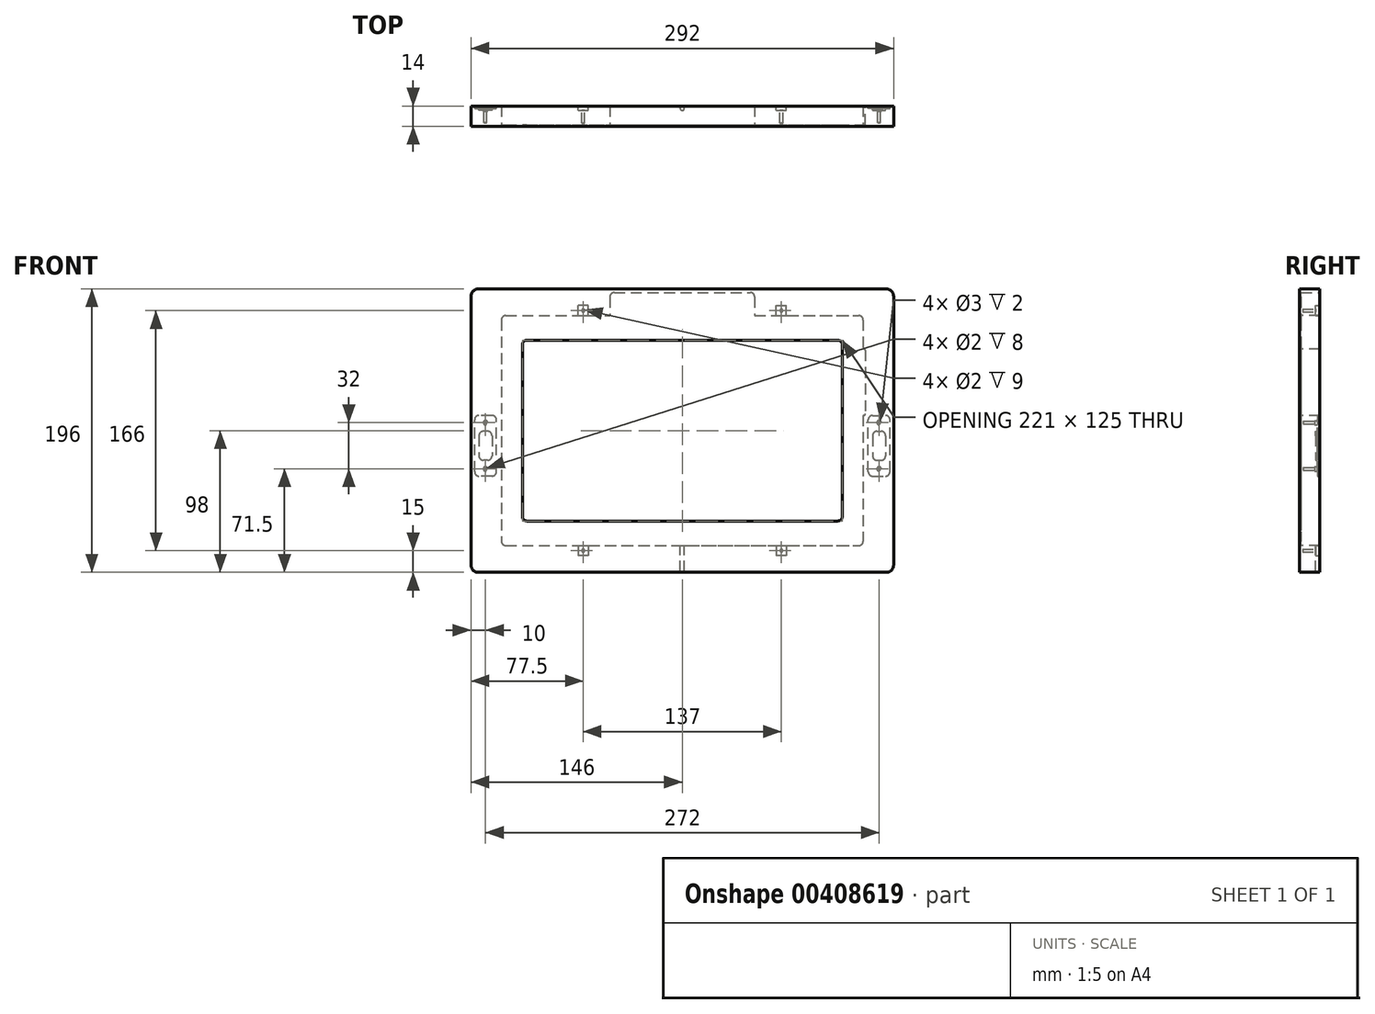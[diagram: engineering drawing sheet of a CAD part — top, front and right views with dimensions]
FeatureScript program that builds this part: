
annotation { "Feature Type Name" : "Feature", "Feature Type Description" : "" }
export const myFeature = defineFeature(function(context is Context, id is Id, definition is map)
    precondition{}
    {
        {
            var Q0;
            Q0=qCreatedBy(makeId("Front.planeOp"),FACE);
            var sketch = newSketch(context, id + "F0", { "sketchPlane" : qUnion([Q0])});
            skLineSegment(sketch, "E0.bottom", {"start": v(-122, 79.5) * mm, "end": v(122, 79.5) * mm});
            skLineSegment(sketch, "E0.top", {"start": v(-122, -79.5) * mm, "end": v(122, -79.5) * mm});
            skLineSegment(sketch, "E0.left", {"start": v(-125, 76.5) * mm, "end": v(-125, -76.5) * mm});
            skLineSegment(sketch, "E0.right", {"start": v(125, 76.5) * mm, "end": v(125, -76.5) * mm});
            skPoint(sketch, "E0.middle", {"position": v(0, 0) * mm});
            skLineSegment(sketch, "E1.bottom", {"start": v(-107.5, 62.5) * mm, "end": v(107.5, 62.5) * mm});
            skLineSegment(sketch, "E1.top", {"start": v(-107.5, -62.5) * mm, "end": v(107.5, -62.5) * mm});
            skLineSegment(sketch, "E1.left", {"start": v(-110.5, 59.5) * mm, "end": v(-110.5, -59.5) * mm});
            skLineSegment(sketch, "E1.right", {"start": v(110.5, 59.5) * mm, "end": v(110.5, -59.5) * mm});
            skLineSegment(sketch, "E2.bottom", {"start": v(-141, 98) * mm, "end": v(141, 98) * mm});
            skLineSegment(sketch, "E2.top", {"start": v(-141, -98) * mm, "end": v(141, -98) * mm});
            skLineSegment(sketch, "E2.left", {"start": v(-146, 93) * mm, "end": v(-146, -93) * mm});
            skLineSegment(sketch, "E2.right", {"start": v(146, 93) * mm, "end": v(146, -93) * mm});
            skPoint(sketch, "E3.visualSharp", {"position": v(146, 98) * mm});
            skArc(sketch, "E3.filletArc", {"start": v(146, 93) * mm, "mid": v(144.54, 96.54) * mm, "end": v(141, 98) * mm});
            skPoint(sketch, "E4.visualSharp", {"position": v(-146, 98) * mm});
            skArc(sketch, "E4.filletArc", {"start": v(-141, 98) * mm, "mid": v(-144.54, 96.54) * mm, "end": v(-146, 93) * mm});
            skPoint(sketch, "E5.visualSharp", {"position": v(-146, -98) * mm});
            skArc(sketch, "E5.filletArc", {"start": v(-146, -93) * mm, "mid": v(-144.54, -96.54) * mm, "end": v(-141, -98) * mm});
            skPoint(sketch, "E6.visualSharp", {"position": v(146, -98) * mm});
            skArc(sketch, "E6.filletArc", {"start": v(141, -98) * mm, "mid": v(144.54, -96.54) * mm, "end": v(146, -93) * mm});
            skPoint(sketch, "E7.visualSharp", {"position": v(125, 79.5) * mm});
            skArc(sketch, "E7.filletArc", {"start": v(125, 76.5) * mm, "mid": v(124.12, 78.62) * mm, "end": v(122, 79.5) * mm});
            skPoint(sketch, "E8.visualSharp", {"position": v(-125, 79.5) * mm});
            skArc(sketch, "E8.filletArc", {"start": v(-122, 79.5) * mm, "mid": v(-124.12, 78.62) * mm, "end": v(-125, 76.5) * mm});
            skPoint(sketch, "E9.visualSharp", {"position": v(-125, -79.5) * mm});
            skArc(sketch, "E9.filletArc", {"start": v(-125, -76.5) * mm, "mid": v(-124.12, -78.62) * mm, "end": v(-122, -79.5) * mm});
            skPoint(sketch, "E10.visualSharp", {"position": v(125, -79.5) * mm});
            skArc(sketch, "E10.filletArc", {"start": v(122, -79.5) * mm, "mid": v(124.12, -78.62) * mm, "end": v(125, -76.5) * mm});
            skPoint(sketch, "E11.visualSharp", {"position": v(110.5, 62.5) * mm});
            skArc(sketch, "E11.filletArc", {"start": v(110.5, 59.5) * mm, "mid": v(109.62, 61.62) * mm, "end": v(107.5, 62.5) * mm});
            skPoint(sketch, "E12.visualSharp", {"position": v(-110.5, 62.5) * mm});
            skArc(sketch, "E12.filletArc", {"start": v(-107.5, 62.5) * mm, "mid": v(-109.62, 61.62) * mm, "end": v(-110.5, 59.5) * mm});
            skPoint(sketch, "E13.visualSharp", {"position": v(-110.5, -62.5) * mm});
            skArc(sketch, "E13.filletArc", {"start": v(-110.5, -59.5) * mm, "mid": v(-109.62, -61.62) * mm, "end": v(-107.5, -62.5) * mm});
            skPoint(sketch, "E14.visualSharp", {"position": v(110.5, -62.5) * mm});
            skArc(sketch, "E14.filletArc", {"start": v(107.5, -62.5) * mm, "mid": v(109.62, -61.62) * mm, "end": v(110.5, -59.5) * mm});
            skSolve(sketch);
        }
        {
            var Q0;
            Q0=makeQuery(id+"F0.imprint","IMPRINT",FACE,{"disambiguationData":[TD([[makeQuery(id+"F0.imprint","IMPRINT",EDGE,{"derivedFrom":sQuery(id+"F0.wireOp",EDGE,"E0.bottom")}),1.0]])]});
            var Q1;
            Q1=makeQuery(id+"F0.imprint","IMPRINT",FACE,{"disambiguationData":[TD([[makeQuery(id+"F0.imprint","IMPRINT",EDGE,{"derivedFrom":sQuery(id+"F0.wireOp",EDGE,"E0.bottom")}),-1.0]])]});
            extrude(context, id + "F1", {"entities" : qUnion([Q0, Q1]), "oppositeDirection" : true, "depth" : 1 * mm});
        }
        {
            var Q0;
            Q0=makeQuery(id+"F0.imprint","IMPRINT",FACE,{"disambiguationData":[TD([[makeQuery(id+"F0.imprint","IMPRINT",EDGE,{"derivedFrom":sQuery(id+"F0.wireOp",EDGE,"E0.bottom")}),1.0]])]});
            extrude(context, id + "F2", {"entities" : qUnion([Q0]), "operationType" : NewBodyOperationType.ADD, "oppositeDirection" : true, "depth" : 14 * mm});
        }
        {
            var Q0;
            Q0=makeQuery(id+"F2.opExtrude","CAP_FACE",FACE,{"disambiguationData":[OSD([sQuery(id+"F0.wireOp",EDGE,"E0.bottom"),sQuery(id+"F0.wireOp",EDGE,"E0.top"),sQuery(id+"F0.wireOp",EDGE,"E0.left"),sQuery(id+"F0.wireOp",EDGE,"E0.right"),sQuery(id+"F0.wireOp",EDGE,"E2.bottom"),sQuery(id+"F0.wireOp",EDGE,"E2.top"),sQuery(id+"F0.wireOp",EDGE,"E2.left"),sQuery(id+"F0.wireOp",EDGE,"E2.right"),sQuery(id+"F0.wireOp",EDGE,"E3.filletArc"),sQuery(id+"F0.wireOp",EDGE,"E4.filletArc"),sQuery(id+"F0.wireOp",EDGE,"E5.filletArc"),sQuery(id+"F0.wireOp",EDGE,"E6.filletArc"),sQuery(id+"F0.wireOp",EDGE,"E7.filletArc"),sQuery(id+"F0.wireOp",EDGE,"E8.filletArc"),sQuery(id+"F0.wireOp",EDGE,"E9.filletArc"),sQuery(id+"F0.wireOp",EDGE,"E10.filletArc")])],"isStart":false});
            var sketch = newSketch(context, id + "F3", { "sketchPlane" : qUnion([Q0])});
            skLineSegment(sketch, "E15.bottom", {"start": v(47, 95.5) * mm, "end": v(-47, 95.5) * mm});
            skLineSegment(sketch, "E15.top", {"start": v(47, 63.5) * mm, "end": v(-47, 63.5) * mm});
            skLineSegment(sketch, "E15.left", {"start": v(50, 92.5) * mm, "end": v(50, 66.5) * mm});
            skLineSegment(sketch, "E15.right", {"start": v(-50, 92.5) * mm, "end": v(-50, 66.5) * mm});
            skPoint(sketch, "E15.middle", {"position": v(0, 79.5) * mm});
            skPoint(sketch, "E16.visualSharp", {"position": v(-50, 95.5) * mm});
            skArc(sketch, "E16.filletArc", {"start": v(-47, 95.5) * mm, "mid": v(-49.12, 94.62) * mm, "end": v(-50, 92.5) * mm});
            skPoint(sketch, "E17.visualSharp", {"position": v(50, 95.5) * mm});
            skArc(sketch, "E17.filletArc", {"start": v(50, 92.5) * mm, "mid": v(49.12, 94.62) * mm, "end": v(47, 95.5) * mm});
            skPoint(sketch, "E18.visualSharp", {"position": v(50, 63.5) * mm});
            skArc(sketch, "E18.filletArc", {"start": v(47, 63.5) * mm, "mid": v(49.12, 64.38) * mm, "end": v(50, 66.5) * mm});
            skPoint(sketch, "E19.visualSharp", {"position": v(-50, 63.5) * mm});
            skArc(sketch, "E19.filletArc", {"start": v(-50, 66.5) * mm, "mid": v(-49.12, 64.38) * mm, "end": v(-47, 63.5) * mm});
            skSolve(sketch);
        }
        {
            var Q0;
            Q0 = qSketchRegion(id + "F3", true);
            extrude(context, id + "F4", {"entities" : qUnion([Q0]), "oppositeDirection" : true, "depth" : 13 * mm});
        }
        {
            var Q0;
            Q0=makeQuery(id+"F4.opExtrude","SWEPT_BODY",BODY,{"disambiguationData":[OSD([sQuery(id+"F3.wireOp",EDGE,"E15.bottom"),sQuery(id+"F3.wireOp",EDGE,"E15.top"),sQuery(id+"F3.wireOp",EDGE,"E15.left"),sQuery(id+"F3.wireOp",EDGE,"E15.right"),sQuery(id+"F3.wireOp",EDGE,"E16.filletArc"),sQuery(id+"F3.wireOp",EDGE,"E17.filletArc"),sQuery(id+"F3.wireOp",EDGE,"E18.filletArc"),sQuery(id+"F3.wireOp",EDGE,"E19.filletArc")])]});
            var Q1;
            Q1=makeQuery(id+"F1.opExtrude","SWEPT_BODY",BODY,{"disambiguationData":[OSD([sQuery(id+"F0.wireOp",EDGE,"E1.bottom"),sQuery(id+"F0.wireOp",EDGE,"E1.top"),sQuery(id+"F0.wireOp",EDGE,"E1.left"),sQuery(id+"F0.wireOp",EDGE,"E1.right"),sQuery(id+"F0.wireOp",EDGE,"E2.bottom"),sQuery(id+"F0.wireOp",EDGE,"E2.top"),sQuery(id+"F0.wireOp",EDGE,"E2.left"),sQuery(id+"F0.wireOp",EDGE,"E2.right"),sQuery(id+"F0.wireOp",EDGE,"E3.filletArc"),sQuery(id+"F0.wireOp",EDGE,"E4.filletArc"),sQuery(id+"F0.wireOp",EDGE,"E5.filletArc"),sQuery(id+"F0.wireOp",EDGE,"E6.filletArc"),sQuery(id+"F0.wireOp",EDGE,"E11.filletArc"),sQuery(id+"F0.wireOp",EDGE,"E12.filletArc"),sQuery(id+"F0.wireOp",EDGE,"E13.filletArc"),sQuery(id+"F0.wireOp",EDGE,"E14.filletArc")])]});
            booleanBodies(context, id + "F5", {"operationType" : BooleanOperationType.SUBTRACTION, "tools" : qUnion([Q0]), "targets" : qUnion([Q1])});
        }
        {
            var Q0;
            Q0=makeQuery(id+"F2.opExtrude","SWEPT_FACE",FACE,{"disambiguationData":[OSD([sQuery(id+"F0.wireOp",EDGE,"E0.top")])]});
            var sketch = newSketch(context, id + "F6", { "sketchPlane" : qUnion([Q0])});
            skLineSegment(sketch, "E20.bottom", {"start": v(0, 11) * mm, "end": v(0, 11) * mm});
            skLineSegment(sketch, "E20.top", {"start": v(-1.5, 17) * mm, "end": v(1.5, 17) * mm});
            skLineSegment(sketch, "E20.left", {"start": v(-1.5, 12.5) * mm, "end": v(-1.5, 17) * mm});
            skLineSegment(sketch, "E20.right", {"start": v(1.5, 12.5) * mm, "end": v(1.5, 17) * mm});
            skPoint(sketch, "E20.middle", {"position": v(0, 14) * mm});
            skPoint(sketch, "E21.visualSharp", {"position": v(1.5, 11) * mm});
            skArc(sketch, "E21.filletArc", {"start": v(0, 11) * mm, "mid": v(1.06, 11.44) * mm, "end": v(1.5, 12.5) * mm});
            skPoint(sketch, "E22.visualSharp", {"position": v(-1.5, 11) * mm});
            skArc(sketch, "E22.filletArc", {"start": v(-1.5, 12.5) * mm, "mid": v(-1.06, 11.44) * mm, "end": v(0, 11) * mm});
            skSolve(sketch);
        }
        {
            var Q0;
            Q0 = qSketchRegion(id + "F6", true);
            extrude(context, id + "F7", {"entities" : qUnion([Q0]), "oppositeDirection" : true, "depth" : 18 * mm});
        }
        {
            var Q0;
            Q0=makeQuery(id+"F7.opExtrude","SWEPT_BODY",BODY,{"disambiguationData":[OSD([sQuery(id+"F6.wireOp",EDGE,"E20.top"),sQuery(id+"F6.wireOp",EDGE,"E20.left"),sQuery(id+"F6.wireOp",EDGE,"E20.right"),sQuery(id+"F6.wireOp",EDGE,"E21.filletArc"),sQuery(id+"F6.wireOp",EDGE,"E22.filletArc")])]});
            var Q1;
            Q1=makeQuery(id+"F1.opExtrude","SWEPT_BODY",BODY,{"disambiguationData":[OSD([sQuery(id+"F0.wireOp",EDGE,"E1.bottom"),sQuery(id+"F0.wireOp",EDGE,"E1.top"),sQuery(id+"F0.wireOp",EDGE,"E1.left"),sQuery(id+"F0.wireOp",EDGE,"E1.right"),sQuery(id+"F0.wireOp",EDGE,"E2.bottom"),sQuery(id+"F0.wireOp",EDGE,"E2.top"),sQuery(id+"F0.wireOp",EDGE,"E2.left"),sQuery(id+"F0.wireOp",EDGE,"E2.right"),sQuery(id+"F0.wireOp",EDGE,"E3.filletArc"),sQuery(id+"F0.wireOp",EDGE,"E4.filletArc"),sQuery(id+"F0.wireOp",EDGE,"E5.filletArc"),sQuery(id+"F0.wireOp",EDGE,"E6.filletArc"),sQuery(id+"F0.wireOp",EDGE,"E11.filletArc"),sQuery(id+"F0.wireOp",EDGE,"E12.filletArc"),sQuery(id+"F0.wireOp",EDGE,"E13.filletArc"),sQuery(id+"F0.wireOp",EDGE,"E14.filletArc")])]});
            booleanBodies(context, id + "F8", {"operationType" : BooleanOperationType.SUBTRACTION, "tools" : qUnion([Q0]), "targets" : qUnion([Q1])});
        }
        {
            var Q0;
            Q0=makeQuery(id+"F2.opExtrude","CAP_FACE",FACE,{"disambiguationData":[OSD([sQuery(id+"F0.wireOp",EDGE,"E0.bottom"),sQuery(id+"F0.wireOp",EDGE,"E0.top"),sQuery(id+"F0.wireOp",EDGE,"E0.left"),sQuery(id+"F0.wireOp",EDGE,"E0.right"),sQuery(id+"F0.wireOp",EDGE,"E2.bottom"),sQuery(id+"F0.wireOp",EDGE,"E2.top"),sQuery(id+"F0.wireOp",EDGE,"E2.left"),sQuery(id+"F0.wireOp",EDGE,"E2.right"),sQuery(id+"F0.wireOp",EDGE,"E3.filletArc"),sQuery(id+"F0.wireOp",EDGE,"E4.filletArc"),sQuery(id+"F0.wireOp",EDGE,"E5.filletArc"),sQuery(id+"F0.wireOp",EDGE,"E6.filletArc"),sQuery(id+"F0.wireOp",EDGE,"E7.filletArc"),sQuery(id+"F0.wireOp",EDGE,"E8.filletArc"),sQuery(id+"F0.wireOp",EDGE,"E9.filletArc"),sQuery(id+"F0.wireOp",EDGE,"E10.filletArc")])],"isStart":false});
            var sketch = newSketch(context, id + "F9", { "sketchPlane" : qUnion([Q0])});
            skLineSegment(sketch, "E23.bottom", {"start": v(-125.5, 56.5) * mm, "end": v(-123.5, 56.5) * mm});
            skLineSegment(sketch, "E23.top", {"start": v(-125.5, 10.5) * mm, "end": v(-123.5, 10.5) * mm});
            skLineSegment(sketch, "E23.left", {"start": v(-126.5, 55.5) * mm, "end": v(-126.5, 11.5) * mm});
            skLineSegment(sketch, "E23.right", {"start": v(-123.5, 56.5) * mm, "end": v(-123.5, 10.5) * mm});
            skPoint(sketch, "E23.middle", {"position": v(-125, 33.5) * mm});
            skPoint(sketch, "E24.visualSharp", {"position": v(-126.5, 56.5) * mm});
            skArc(sketch, "E24.filletArc", {"start": v(-125.5, 56.5) * mm, "mid": v(-126.2, 56.2) * mm, "end": v(-126.5, 55.5) * mm});
            skPoint(sketch, "E25.visualSharp", {"position": v(-126.5, 10.5) * mm});
            skArc(sketch, "E25.filletArc", {"start": v(-126.5, 11.5) * mm, "mid": v(-126.2, 10.8) * mm, "end": v(-125.5, 10.5) * mm});
            skSolve(sketch);
        }
        {
            var Q0;
            Q0 = qSketchRegion(id + "F9", true);
            extrude(context, id + "F10", {"entities" : qUnion([Q0]), "oppositeDirection" : true, "depth" : 13 * mm});
        }
        {
            var Q0;
            Q0=makeQuery(id+"F10.opExtrude","SWEPT_BODY",BODY,{"disambiguationData":[OSD([sQuery(id+"F9.wireOp",EDGE,"E23.bottom"),sQuery(id+"F9.wireOp",EDGE,"E23.top"),sQuery(id+"F9.wireOp",EDGE,"E23.left"),sQuery(id+"F9.wireOp",EDGE,"E23.right"),sQuery(id+"F9.wireOp",EDGE,"E24.filletArc"),sQuery(id+"F9.wireOp",EDGE,"E25.filletArc")])]});
            var Q1;
            Q1=makeQuery(id+"F1.opExtrude","SWEPT_BODY",BODY,{"disambiguationData":[OSD([sQuery(id+"F0.wireOp",EDGE,"E1.bottom"),sQuery(id+"F0.wireOp",EDGE,"E1.top"),sQuery(id+"F0.wireOp",EDGE,"E1.left"),sQuery(id+"F0.wireOp",EDGE,"E1.right"),sQuery(id+"F0.wireOp",EDGE,"E2.bottom"),sQuery(id+"F0.wireOp",EDGE,"E2.top"),sQuery(id+"F0.wireOp",EDGE,"E2.left"),sQuery(id+"F0.wireOp",EDGE,"E2.right"),sQuery(id+"F0.wireOp",EDGE,"E3.filletArc"),sQuery(id+"F0.wireOp",EDGE,"E4.filletArc"),sQuery(id+"F0.wireOp",EDGE,"E5.filletArc"),sQuery(id+"F0.wireOp",EDGE,"E6.filletArc"),sQuery(id+"F0.wireOp",EDGE,"E11.filletArc"),sQuery(id+"F0.wireOp",EDGE,"E12.filletArc"),sQuery(id+"F0.wireOp",EDGE,"E13.filletArc"),sQuery(id+"F0.wireOp",EDGE,"E14.filletArc")])]});
            booleanBodies(context, id + "F11", {"operationType" : BooleanOperationType.SUBTRACTION, "tools" : qUnion([Q0]), "targets" : qUnion([Q1])});
        }
        {
            var Q0;
            Q0=makeQuery(id+"F2.opExtrude","CAP_FACE",FACE,{"disambiguationData":[OSD([sQuery(id+"F0.wireOp",EDGE,"E0.bottom"),sQuery(id+"F0.wireOp",EDGE,"E0.top"),sQuery(id+"F0.wireOp",EDGE,"E0.left"),sQuery(id+"F0.wireOp",EDGE,"E0.right"),sQuery(id+"F0.wireOp",EDGE,"E2.bottom"),sQuery(id+"F0.wireOp",EDGE,"E2.top"),sQuery(id+"F0.wireOp",EDGE,"E2.left"),sQuery(id+"F0.wireOp",EDGE,"E2.right"),sQuery(id+"F0.wireOp",EDGE,"E3.filletArc"),sQuery(id+"F0.wireOp",EDGE,"E4.filletArc"),sQuery(id+"F0.wireOp",EDGE,"E5.filletArc"),sQuery(id+"F0.wireOp",EDGE,"E6.filletArc"),sQuery(id+"F0.wireOp",EDGE,"E7.filletArc"),sQuery(id+"F0.wireOp",EDGE,"E8.filletArc"),sQuery(id+"F0.wireOp",EDGE,"E9.filletArc"),sQuery(id+"F0.wireOp",EDGE,"E10.filletArc")])],"isStart":false});
            var sketch = newSketch(context, id + "F12", { "sketchPlane" : qUnion([Q0])});
            skLineSegment(sketch, "E26.bottom", {"start": v(-131.5, -31.5) * mm, "end": v(-140.5, -31.5) * mm});
            skLineSegment(sketch, "E26.top", {"start": v(-131.5, 10.5) * mm, "end": v(-140.5, 10.5) * mm});
            skLineSegment(sketch, "E26.left", {"start": v(-128.5, -28.5) * mm, "end": v(-128.5, 7.5) * mm});
            skLineSegment(sketch, "E26.right", {"start": v(-143.5, -28.5) * mm, "end": v(-143.5, 7.5) * mm});
            skPoint(sketch, "E26.middle", {"position": v(-136, -10.5) * mm});
            skPoint(sketch, "E27.visualSharp", {"position": v(-143.5, 10.5) * mm});
            skArc(sketch, "E27.filletArc", {"start": v(-140.5, 10.5) * mm, "mid": v(-142.62, 9.62) * mm, "end": v(-143.5, 7.5) * mm});
            skPoint(sketch, "E28.visualSharp", {"position": v(-128.5, 10.5) * mm});
            skArc(sketch, "E28.filletArc", {"start": v(-128.5, 7.5) * mm, "mid": v(-129.38, 9.62) * mm, "end": v(-131.5, 10.5) * mm});
            skPoint(sketch, "E29.visualSharp", {"position": v(-143.5, -31.5) * mm});
            skArc(sketch, "E29.filletArc", {"start": v(-143.5, -28.5) * mm, "mid": v(-142.62, -30.62) * mm, "end": v(-140.5, -31.5) * mm});
            skPoint(sketch, "E30.visualSharp", {"position": v(-128.5, -31.5) * mm});
            skArc(sketch, "E30.filletArc", {"start": v(-131.5, -31.5) * mm, "mid": v(-129.38, -30.62) * mm, "end": v(-128.5, -28.5) * mm});
            skLineSegment(sketch, "E31.bottom", {"start": v(131.5, -31.5) * mm, "end": v(140.5, -31.5) * mm});
            skLineSegment(sketch, "E31.top", {"start": v(131.5, 10.5) * mm, "end": v(140.5, 10.5) * mm});
            skLineSegment(sketch, "E31.left", {"start": v(128.5, -28.5) * mm, "end": v(128.5, 7.5) * mm});
            skLineSegment(sketch, "E31.right", {"start": v(143.5, -28.5) * mm, "end": v(143.5, 7.5) * mm});
            skPoint(sketch, "E31.middle", {"position": v(136, -10.5) * mm});
            skPoint(sketch, "E32.visualSharp", {"position": v(128.5, 10.5) * mm});
            skArc(sketch, "E32.filletArc", {"start": v(131.5, 10.5) * mm, "mid": v(129.38, 9.62) * mm, "end": v(128.5, 7.5) * mm});
            skPoint(sketch, "E33.visualSharp", {"position": v(143.5, 10.5) * mm});
            skArc(sketch, "E33.filletArc", {"start": v(143.5, 7.5) * mm, "mid": v(142.62, 9.62) * mm, "end": v(140.5, 10.5) * mm});
            skPoint(sketch, "E34.visualSharp", {"position": v(143.5, -31.5) * mm});
            skArc(sketch, "E34.filletArc", {"start": v(140.5, -31.5) * mm, "mid": v(142.62, -30.62) * mm, "end": v(143.5, -28.5) * mm});
            skPoint(sketch, "E35.visualSharp", {"position": v(128.5, -31.5) * mm});
            skArc(sketch, "E35.filletArc", {"start": v(128.5, -28.5) * mm, "mid": v(129.38, -30.62) * mm, "end": v(131.5, -31.5) * mm});
            skSolve(sketch);
        }
        {
            var Q0;
            Q0 = qSketchRegion(id + "F12", true);
            extrude(context, id + "F13", {"entities" : qUnion([Q0]), "oppositeDirection" : true, "depth" : 1.59 * mm});
        }
        {
            var Q0;
            Q0=makeQuery(id+"F13.opExtrude","SWEPT_BODY",BODY,{"disambiguationData":[OSD([sQuery(id+"F12.wireOp",EDGE,"E26.bottom"),sQuery(id+"F12.wireOp",EDGE,"E26.top"),sQuery(id+"F12.wireOp",EDGE,"E26.left"),sQuery(id+"F12.wireOp",EDGE,"E26.right"),sQuery(id+"F12.wireOp",EDGE,"E27.filletArc"),sQuery(id+"F12.wireOp",EDGE,"E28.filletArc"),sQuery(id+"F12.wireOp",EDGE,"E29.filletArc"),sQuery(id+"F12.wireOp",EDGE,"E30.filletArc")])]});
            var Q1;
            Q1=makeQuery(id+"F13.opExtrude","SWEPT_BODY",BODY,{"disambiguationData":[OSD([sQuery(id+"F12.wireOp",EDGE,"E31.bottom"),sQuery(id+"F12.wireOp",EDGE,"E31.top"),sQuery(id+"F12.wireOp",EDGE,"E31.left"),sQuery(id+"F12.wireOp",EDGE,"E31.right"),sQuery(id+"F12.wireOp",EDGE,"E32.filletArc"),sQuery(id+"F12.wireOp",EDGE,"E33.filletArc"),sQuery(id+"F12.wireOp",EDGE,"E34.filletArc"),sQuery(id+"F12.wireOp",EDGE,"E35.filletArc")])]});
            var Q2;
            Q2=makeQuery(id+"F1.opExtrude","SWEPT_BODY",BODY,{"disambiguationData":[OSD([sQuery(id+"F0.wireOp",EDGE,"E1.bottom"),sQuery(id+"F0.wireOp",EDGE,"E1.top"),sQuery(id+"F0.wireOp",EDGE,"E1.left"),sQuery(id+"F0.wireOp",EDGE,"E1.right"),sQuery(id+"F0.wireOp",EDGE,"E2.bottom"),sQuery(id+"F0.wireOp",EDGE,"E2.top"),sQuery(id+"F0.wireOp",EDGE,"E2.left"),sQuery(id+"F0.wireOp",EDGE,"E2.right"),sQuery(id+"F0.wireOp",EDGE,"E3.filletArc"),sQuery(id+"F0.wireOp",EDGE,"E4.filletArc"),sQuery(id+"F0.wireOp",EDGE,"E5.filletArc"),sQuery(id+"F0.wireOp",EDGE,"E6.filletArc"),sQuery(id+"F0.wireOp",EDGE,"E11.filletArc"),sQuery(id+"F0.wireOp",EDGE,"E12.filletArc"),sQuery(id+"F0.wireOp",EDGE,"E13.filletArc"),sQuery(id+"F0.wireOp",EDGE,"E14.filletArc")])]});
            booleanBodies(context, id + "F14", {"operationType" : BooleanOperationType.SUBTRACTION, "tools" : qUnion([Q0, Q1]), "targets" : qUnion([Q2])});
        }
        {
            var Q0;
            Q0=makeQuery(id+"F14.opBoolean","COPY",FACE,{"derivedFrom":makeQuery(id+"F13.opExtrude","CAP_FACE",FACE,{"disambiguationData":[OSD([sQuery(id+"F12.wireOp",EDGE,"E26.bottom"),sQuery(id+"F12.wireOp",EDGE,"E26.top"),sQuery(id+"F12.wireOp",EDGE,"E26.left"),sQuery(id+"F12.wireOp",EDGE,"E26.right"),sQuery(id+"F12.wireOp",EDGE,"E27.filletArc"),sQuery(id+"F12.wireOp",EDGE,"E28.filletArc"),sQuery(id+"F12.wireOp",EDGE,"E29.filletArc"),sQuery(id+"F12.wireOp",EDGE,"E30.filletArc")])],"isStart":false})});
            var sketch = newSketch(context, id + "F15", { "sketchPlane" : qUnion([Q0])});
            skLineSegment(sketch, "E36.bottom", {"start": v(-134.5, -0.5) * mm, "end": v(-137.5, -0.5) * mm});
            skLineSegment(sketch, "E36.top", {"start": v(-134.5, -20.5) * mm, "end": v(-137.5, -20.5) * mm});
            skLineSegment(sketch, "E36.left", {"start": v(-131.5, -3.5) * mm, "end": v(-131.5, -17.5) * mm});
            skLineSegment(sketch, "E36.right", {"start": v(-140.5, -3.5) * mm, "end": v(-140.5, -17.5) * mm});
            skPoint(sketch, "E36.middle", {"position": v(-136, -10.5) * mm});
            skPoint(sketch, "E37.visualSharp", {"position": v(-140.5, -0.5) * mm});
            skArc(sketch, "E37.filletArc", {"start": v(-137.5, -0.5) * mm, "mid": v(-139.62, -1.38) * mm, "end": v(-140.5, -3.5) * mm});
            skPoint(sketch, "E38.visualSharp", {"position": v(-131.5, -0.5) * mm});
            skArc(sketch, "E38.filletArc", {"start": v(-131.5, -3.5) * mm, "mid": v(-132.38, -1.38) * mm, "end": v(-134.5, -0.5) * mm});
            skPoint(sketch, "E39.visualSharp", {"position": v(-131.5, -20.5) * mm});
            skArc(sketch, "E39.filletArc", {"start": v(-134.5, -20.5) * mm, "mid": v(-132.38, -19.62) * mm, "end": v(-131.5, -17.5) * mm});
            skPoint(sketch, "E40.visualSharp", {"position": v(-140.5, -20.5) * mm});
            skArc(sketch, "E40.filletArc", {"start": v(-140.5, -17.5) * mm, "mid": v(-139.62, -19.62) * mm, "end": v(-137.5, -20.5) * mm});
            skLineSegment(sketch, "E41.bottom", {"start": v(134.5, -0.5) * mm, "end": v(137.5, -0.5) * mm});
            skLineSegment(sketch, "E41.top", {"start": v(134.5, -20.5) * mm, "end": v(137.5, -20.5) * mm});
            skLineSegment(sketch, "E41.left", {"start": v(131.5, -3.5) * mm, "end": v(131.5, -17.5) * mm});
            skLineSegment(sketch, "E41.right", {"start": v(140.5, -3.5) * mm, "end": v(140.5, -17.5) * mm});
            skPoint(sketch, "E41.middle", {"position": v(136, -10.5) * mm});
            skPoint(sketch, "E42.visualSharp", {"position": v(131.5, -0.5) * mm});
            skArc(sketch, "E42.filletArc", {"start": v(134.5, -0.5) * mm, "mid": v(132.38, -1.38) * mm, "end": v(131.5, -3.5) * mm});
            skPoint(sketch, "E43.visualSharp", {"position": v(131.5, -20.5) * mm});
            skArc(sketch, "E43.filletArc", {"start": v(131.5, -17.5) * mm, "mid": v(132.38, -19.62) * mm, "end": v(134.5, -20.5) * mm});
            skPoint(sketch, "E44.visualSharp", {"position": v(140.5, -20.5) * mm});
            skArc(sketch, "E44.filletArc", {"start": v(137.5, -20.5) * mm, "mid": v(139.62, -19.62) * mm, "end": v(140.5, -17.5) * mm});
            skPoint(sketch, "E45.visualSharp", {"position": v(140.5, -0.5) * mm});
            skArc(sketch, "E45.filletArc", {"start": v(140.5, -3.5) * mm, "mid": v(139.62, -1.38) * mm, "end": v(137.5, -0.5) * mm});
            skSolve(sketch);
        }
        {
            var Q0;
            Q0 = qSketchRegion(id + "F15", true);
            extrude(context, id + "F16", {"entities" : qUnion([Q0]), "oppositeDirection" : true, "depth" : 1.5 * mm});
        }
        {
            var Q0;
            Q0=makeQuery(id+"F16.opExtrude","SWEPT_BODY",BODY,{"disambiguationData":[OSD([sQuery(id+"F15.wireOp",EDGE,"E36.bottom"),sQuery(id+"F15.wireOp",EDGE,"E36.top"),sQuery(id+"F15.wireOp",EDGE,"E36.left"),sQuery(id+"F15.wireOp",EDGE,"E36.right"),sQuery(id+"F15.wireOp",EDGE,"E37.filletArc"),sQuery(id+"F15.wireOp",EDGE,"E38.filletArc"),sQuery(id+"F15.wireOp",EDGE,"E39.filletArc"),sQuery(id+"F15.wireOp",EDGE,"E40.filletArc")])]});
            var Q1;
            Q1=makeQuery(id+"F16.opExtrude","SWEPT_BODY",BODY,{"disambiguationData":[OSD([sQuery(id+"F15.wireOp",EDGE,"E41.bottom"),sQuery(id+"F15.wireOp",EDGE,"E41.top"),sQuery(id+"F15.wireOp",EDGE,"E41.left"),sQuery(id+"F15.wireOp",EDGE,"E41.right"),sQuery(id+"F15.wireOp",EDGE,"E42.filletArc"),sQuery(id+"F15.wireOp",EDGE,"E43.filletArc"),sQuery(id+"F15.wireOp",EDGE,"E44.filletArc"),sQuery(id+"F15.wireOp",EDGE,"E45.filletArc")])]});
            var Q2;
            Q2=makeQuery(id+"F1.opExtrude","SWEPT_BODY",BODY,{"disambiguationData":[OSD([sQuery(id+"F0.wireOp",EDGE,"E1.bottom"),sQuery(id+"F0.wireOp",EDGE,"E1.top"),sQuery(id+"F0.wireOp",EDGE,"E1.left"),sQuery(id+"F0.wireOp",EDGE,"E1.right"),sQuery(id+"F0.wireOp",EDGE,"E2.bottom"),sQuery(id+"F0.wireOp",EDGE,"E2.top"),sQuery(id+"F0.wireOp",EDGE,"E2.left"),sQuery(id+"F0.wireOp",EDGE,"E2.right"),sQuery(id+"F0.wireOp",EDGE,"E3.filletArc"),sQuery(id+"F0.wireOp",EDGE,"E4.filletArc"),sQuery(id+"F0.wireOp",EDGE,"E5.filletArc"),sQuery(id+"F0.wireOp",EDGE,"E6.filletArc"),sQuery(id+"F0.wireOp",EDGE,"E11.filletArc"),sQuery(id+"F0.wireOp",EDGE,"E12.filletArc"),sQuery(id+"F0.wireOp",EDGE,"E13.filletArc"),sQuery(id+"F0.wireOp",EDGE,"E14.filletArc")])]});
            booleanBodies(context, id + "F17", {"operationType" : BooleanOperationType.SUBTRACTION, "tools" : qUnion([Q0, Q1]), "targets" : qUnion([Q2])});
        }
        {
            var Q0;
            Q0=makeQuery(id+"F14.opBoolean","COPY",FACE,{"derivedFrom":makeQuery(id+"F13.opExtrude","CAP_FACE",FACE,{"disambiguationData":[OSD([sQuery(id+"F12.wireOp",EDGE,"E26.bottom"),sQuery(id+"F12.wireOp",EDGE,"E26.top"),sQuery(id+"F12.wireOp",EDGE,"E26.left"),sQuery(id+"F12.wireOp",EDGE,"E26.right"),sQuery(id+"F12.wireOp",EDGE,"E27.filletArc"),sQuery(id+"F12.wireOp",EDGE,"E28.filletArc"),sQuery(id+"F12.wireOp",EDGE,"E29.filletArc"),sQuery(id+"F12.wireOp",EDGE,"E30.filletArc")])],"isStart":false})});
            var sketch = newSketch(context, id + "F18", { "sketchPlane" : qUnion([Q0])});
            skCircle(sketch, "E46", {"center": v(-136, 5.5) * mm, "radius": 1 * mm});
            skCircle(sketch, "E47", {"center": v(-136, -26.5) * mm, "radius": 1 * mm});
            skCircle(sketch, "E48", {"center": v(136, 5.5) * mm, "radius": 1 * mm});
            skCircle(sketch, "E49", {"center": v(136, -26.5) * mm, "radius": 1 * mm});
            skSolve(sketch);
        }
        {
            var Q0;
            Q0 = qSketchRegion(id + "F18", true);
            extrude(context, id + "F19", {"entities" : qUnion([Q0]), "oppositeDirection" : true, "depth" : 10 * mm});
        }
        {
            var Q0;
            Q0=makeQuery(id+"F19.opExtrude","SWEPT_BODY",BODY,{"disambiguationData":[OSD([sQuery(id+"F18.wireOp",EDGE,"E46")])]});
            var Q1;
            Q1=makeQuery(id+"F19.opExtrude","SWEPT_BODY",BODY,{"disambiguationData":[OSD([sQuery(id+"F18.wireOp",EDGE,"E47")])]});
            var Q2;
            Q2=makeQuery(id+"F19.opExtrude","SWEPT_BODY",BODY,{"disambiguationData":[OSD([sQuery(id+"F18.wireOp",EDGE,"E48")])]});
            var Q3;
            Q3=makeQuery(id+"F19.opExtrude","SWEPT_BODY",BODY,{"disambiguationData":[OSD([sQuery(id+"F18.wireOp",EDGE,"E49")])]});
            var Q4;
            Q4=makeQuery(id+"F1.opExtrude","SWEPT_BODY",BODY,{"disambiguationData":[OSD([sQuery(id+"F0.wireOp",EDGE,"E1.bottom"),sQuery(id+"F0.wireOp",EDGE,"E1.top"),sQuery(id+"F0.wireOp",EDGE,"E1.left"),sQuery(id+"F0.wireOp",EDGE,"E1.right"),sQuery(id+"F0.wireOp",EDGE,"E2.bottom"),sQuery(id+"F0.wireOp",EDGE,"E2.top"),sQuery(id+"F0.wireOp",EDGE,"E2.left"),sQuery(id+"F0.wireOp",EDGE,"E2.right"),sQuery(id+"F0.wireOp",EDGE,"E3.filletArc"),sQuery(id+"F0.wireOp",EDGE,"E4.filletArc"),sQuery(id+"F0.wireOp",EDGE,"E5.filletArc"),sQuery(id+"F0.wireOp",EDGE,"E6.filletArc"),sQuery(id+"F0.wireOp",EDGE,"E11.filletArc"),sQuery(id+"F0.wireOp",EDGE,"E12.filletArc"),sQuery(id+"F0.wireOp",EDGE,"E13.filletArc"),sQuery(id+"F0.wireOp",EDGE,"E14.filletArc")])]});
            booleanBodies(context, id + "F20", {"operationType" : BooleanOperationType.SUBTRACTION, "tools" : qUnion([Q0, Q1, Q2, Q3]), "targets" : qUnion([Q4])});
        }
        {
            var Q0;
            Q0=makeQuery(id+"F14.opBoolean","COPY",FACE,{"derivedFrom":makeQuery(id+"F13.opExtrude","CAP_FACE",FACE,{"disambiguationData":[OSD([sQuery(id+"F12.wireOp",EDGE,"E26.bottom"),sQuery(id+"F12.wireOp",EDGE,"E26.top"),sQuery(id+"F12.wireOp",EDGE,"E26.left"),sQuery(id+"F12.wireOp",EDGE,"E26.right"),sQuery(id+"F12.wireOp",EDGE,"E27.filletArc"),sQuery(id+"F12.wireOp",EDGE,"E28.filletArc"),sQuery(id+"F12.wireOp",EDGE,"E29.filletArc"),sQuery(id+"F12.wireOp",EDGE,"E30.filletArc")])],"isStart":false})});
            var sketch = newSketch(context, id + "F21", { "sketchPlane" : qUnion([Q0])});
            skCircle(sketch, "E50", {"center": v(-136, 5.5) * mm, "radius": 1.5 * mm});
            skCircle(sketch, "E51", {"center": v(-136, -26.5) * mm, "radius": 1.5 * mm});
            skCircle(sketch, "E52", {"center": v(136, -26.5) * mm, "radius": 1.5 * mm});
            skCircle(sketch, "E53", {"center": v(136, 5.5) * mm, "radius": 1.5 * mm});
            skSolve(sketch);
        }
        {
            var Q0;
            Q0 = qSketchRegion(id + "F21", true);
            extrude(context, id + "F22", {"entities" : qUnion([Q0]), "oppositeDirection" : true, "depth" : 2 * mm});
        }
        {
            var Q0;
            Q0=makeQuery(id+"F22.opExtrude","SWEPT_BODY",BODY,{"disambiguationData":[OSD([sQuery(id+"F21.wireOp",EDGE,"E50")])]});
            var Q1;
            Q1=makeQuery(id+"F22.opExtrude","SWEPT_BODY",BODY,{"disambiguationData":[OSD([sQuery(id+"F21.wireOp",EDGE,"E51")])]});
            var Q2;
            Q2=makeQuery(id+"F22.opExtrude","SWEPT_BODY",BODY,{"disambiguationData":[OSD([sQuery(id+"F21.wireOp",EDGE,"E52")])]});
            var Q3;
            Q3=makeQuery(id+"F22.opExtrude","SWEPT_BODY",BODY,{"disambiguationData":[OSD([sQuery(id+"F21.wireOp",EDGE,"E53")])]});
            var Q4;
            Q4=makeQuery(id+"F1.opExtrude","SWEPT_BODY",BODY,{"disambiguationData":[OSD([sQuery(id+"F0.wireOp",EDGE,"E1.bottom"),sQuery(id+"F0.wireOp",EDGE,"E1.top"),sQuery(id+"F0.wireOp",EDGE,"E1.left"),sQuery(id+"F0.wireOp",EDGE,"E1.right"),sQuery(id+"F0.wireOp",EDGE,"E2.bottom"),sQuery(id+"F0.wireOp",EDGE,"E2.top"),sQuery(id+"F0.wireOp",EDGE,"E2.left"),sQuery(id+"F0.wireOp",EDGE,"E2.right"),sQuery(id+"F0.wireOp",EDGE,"E3.filletArc"),sQuery(id+"F0.wireOp",EDGE,"E4.filletArc"),sQuery(id+"F0.wireOp",EDGE,"E5.filletArc"),sQuery(id+"F0.wireOp",EDGE,"E6.filletArc"),sQuery(id+"F0.wireOp",EDGE,"E11.filletArc"),sQuery(id+"F0.wireOp",EDGE,"E12.filletArc"),sQuery(id+"F0.wireOp",EDGE,"E13.filletArc"),sQuery(id+"F0.wireOp",EDGE,"E14.filletArc")])]});
            booleanBodies(context, id + "F23", {"operationType" : BooleanOperationType.SUBTRACTION, "tools" : qUnion([Q0, Q1, Q2, Q3]), "targets" : qUnion([Q4])});
        }
        {
            var Q0;
            Q0=makeQuery(id+"F2.opExtrude","CAP_FACE",FACE,{"disambiguationData":[OSD([sQuery(id+"F0.wireOp",EDGE,"E0.bottom"),sQuery(id+"F0.wireOp",EDGE,"E0.top"),sQuery(id+"F0.wireOp",EDGE,"E0.left"),sQuery(id+"F0.wireOp",EDGE,"E0.right"),sQuery(id+"F0.wireOp",EDGE,"E2.bottom"),sQuery(id+"F0.wireOp",EDGE,"E2.top"),sQuery(id+"F0.wireOp",EDGE,"E2.left"),sQuery(id+"F0.wireOp",EDGE,"E2.right"),sQuery(id+"F0.wireOp",EDGE,"E3.filletArc"),sQuery(id+"F0.wireOp",EDGE,"E4.filletArc"),sQuery(id+"F0.wireOp",EDGE,"E5.filletArc"),sQuery(id+"F0.wireOp",EDGE,"E6.filletArc"),sQuery(id+"F0.wireOp",EDGE,"E7.filletArc"),sQuery(id+"F0.wireOp",EDGE,"E8.filletArc"),sQuery(id+"F0.wireOp",EDGE,"E9.filletArc"),sQuery(id+"F0.wireOp",EDGE,"E10.filletArc")])],"isStart":false});
            var sketch = newSketch(context, id + "F24", { "sketchPlane" : qUnion([Q0])});
            skLineSegment(sketch, "E54.bottom", {"start": v(-65, 79.5) * mm, "end": v(-72, 79.5) * mm});
            skLineSegment(sketch, "E54.top", {"start": v(-65, 86.5) * mm, "end": v(-72, 86.5) * mm});
            skLineSegment(sketch, "E54.left", {"start": v(-65, 79.5) * mm, "end": v(-65, 86.5) * mm});
            skLineSegment(sketch, "E54.right", {"start": v(-72, 79.5) * mm, "end": v(-72, 86.5) * mm});
            skLineSegment(sketch, "E55.bottom", {"start": v(65, 79.5) * mm, "end": v(72, 79.5) * mm});
            skLineSegment(sketch, "E55.top", {"start": v(65, 86.5) * mm, "end": v(72, 86.5) * mm});
            skLineSegment(sketch, "E55.left", {"start": v(65, 79.5) * mm, "end": v(65, 86.5) * mm});
            skLineSegment(sketch, "E55.right", {"start": v(72, 79.5) * mm, "end": v(72, 86.5) * mm});
            skLineSegment(sketch, "E56.bottom", {"start": v(-72, -79.5) * mm, "end": v(-65, -79.5) * mm});
            skLineSegment(sketch, "E56.top", {"start": v(-72, -86.5) * mm, "end": v(-65, -86.5) * mm});
            skLineSegment(sketch, "E56.left", {"start": v(-72, -79.5) * mm, "end": v(-72, -86.5) * mm});
            skLineSegment(sketch, "E56.right", {"start": v(-65, -79.5) * mm, "end": v(-65, -86.5) * mm});
            skLineSegment(sketch, "E57.bottom", {"start": v(65, -79.5) * mm, "end": v(72, -79.5) * mm});
            skLineSegment(sketch, "E57.top", {"start": v(65, -86.5) * mm, "end": v(72, -86.5) * mm});
            skLineSegment(sketch, "E57.left", {"start": v(65, -79.5) * mm, "end": v(65, -86.5) * mm});
            skLineSegment(sketch, "E57.right", {"start": v(72, -79.5) * mm, "end": v(72, -86.5) * mm});
            skSolve(sketch);
        }
        {
            var Q0;
            Q0 = qSketchRegion(id + "F24", true);
            extrude(context, id + "F25", {"entities" : qUnion([Q0]), "oppositeDirection" : true, "depth" : 3 * mm});
        }
        {
            var Q0;
            Q0=makeQuery(id+"F25.opExtrude","SWEPT_BODY",BODY,{"disambiguationData":[OSD([sQuery(id+"F24.wireOp",EDGE,"E54.bottom"),sQuery(id+"F24.wireOp",EDGE,"E54.top"),sQuery(id+"F24.wireOp",EDGE,"E54.left"),sQuery(id+"F24.wireOp",EDGE,"E54.right")])]});
            var Q1;
            Q1=makeQuery(id+"F25.opExtrude","SWEPT_BODY",BODY,{"disambiguationData":[OSD([sQuery(id+"F24.wireOp",EDGE,"E55.bottom"),sQuery(id+"F24.wireOp",EDGE,"E55.top"),sQuery(id+"F24.wireOp",EDGE,"E55.left"),sQuery(id+"F24.wireOp",EDGE,"E55.right")])]});
            var Q2;
            Q2=makeQuery(id+"F25.opExtrude","SWEPT_BODY",BODY,{"disambiguationData":[OSD([sQuery(id+"F24.wireOp",EDGE,"E56.bottom"),sQuery(id+"F24.wireOp",EDGE,"E56.top"),sQuery(id+"F24.wireOp",EDGE,"E56.left"),sQuery(id+"F24.wireOp",EDGE,"E56.right")])]});
            var Q3;
            Q3=makeQuery(id+"F25.opExtrude","SWEPT_BODY",BODY,{"disambiguationData":[OSD([sQuery(id+"F24.wireOp",EDGE,"E57.bottom"),sQuery(id+"F24.wireOp",EDGE,"E57.top"),sQuery(id+"F24.wireOp",EDGE,"E57.left"),sQuery(id+"F24.wireOp",EDGE,"E57.right")])]});
            var Q4;
            Q4=makeQuery(id+"F1.opExtrude","SWEPT_BODY",BODY,{"disambiguationData":[OSD([sQuery(id+"F0.wireOp",EDGE,"E1.bottom"),sQuery(id+"F0.wireOp",EDGE,"E1.top"),sQuery(id+"F0.wireOp",EDGE,"E1.left"),sQuery(id+"F0.wireOp",EDGE,"E1.right"),sQuery(id+"F0.wireOp",EDGE,"E2.bottom"),sQuery(id+"F0.wireOp",EDGE,"E2.top"),sQuery(id+"F0.wireOp",EDGE,"E2.left"),sQuery(id+"F0.wireOp",EDGE,"E2.right"),sQuery(id+"F0.wireOp",EDGE,"E3.filletArc"),sQuery(id+"F0.wireOp",EDGE,"E4.filletArc"),sQuery(id+"F0.wireOp",EDGE,"E5.filletArc"),sQuery(id+"F0.wireOp",EDGE,"E6.filletArc"),sQuery(id+"F0.wireOp",EDGE,"E11.filletArc"),sQuery(id+"F0.wireOp",EDGE,"E12.filletArc"),sQuery(id+"F0.wireOp",EDGE,"E13.filletArc"),sQuery(id+"F0.wireOp",EDGE,"E14.filletArc")])]});
            booleanBodies(context, id + "F26", {"operationType" : BooleanOperationType.SUBTRACTION, "tools" : qUnion([Q0, Q1, Q2, Q3]), "targets" : qUnion([Q4])});
        }
        {
            var Q0;
            Q0=makeQuery(id+"F26.opBoolean","COPY",FACE,{"derivedFrom":makeQuery(id+"F25.opExtrude","CAP_FACE",FACE,{"disambiguationData":[OSD([sQuery(id+"F24.wireOp",EDGE,"E54.bottom"),sQuery(id+"F24.wireOp",EDGE,"E54.top"),sQuery(id+"F24.wireOp",EDGE,"E54.left"),sQuery(id+"F24.wireOp",EDGE,"E54.right")])],"isStart":false})});
            var sketch = newSketch(context, id + "F27", { "sketchPlane" : qUnion([Q0])});
            skCircle(sketch, "E58", {"center": v(-68.5, 83) * mm, "radius": 1 * mm});
            skCircle(sketch, "E59", {"center": v(68.5, 83) * mm, "radius": 1 * mm});
            skCircle(sketch, "E60", {"center": v(-68.5, -83) * mm, "radius": 1 * mm});
            skCircle(sketch, "E61", {"center": v(68.5, -83) * mm, "radius": 1 * mm});
            skSolve(sketch);
        }
        {
            var Q0;
            Q0 = qSketchRegion(id + "F27", true);
            extrude(context, id + "F28", {"entities" : qUnion([Q0]), "oppositeDirection" : true, "depth" : 9 * mm});
        }
        {
            var Q0;
            Q0=makeQuery(id+"F28.opExtrude","SWEPT_BODY",BODY,{"disambiguationData":[OSD([sQuery(id+"F27.wireOp",EDGE,"E58")])]});
            var Q1;
            Q1=makeQuery(id+"F28.opExtrude","SWEPT_BODY",BODY,{"disambiguationData":[OSD([sQuery(id+"F27.wireOp",EDGE,"E59")])]});
            var Q2;
            Q2=makeQuery(id+"F28.opExtrude","SWEPT_BODY",BODY,{"disambiguationData":[OSD([sQuery(id+"F27.wireOp",EDGE,"E60")])]});
            var Q3;
            Q3=makeQuery(id+"F28.opExtrude","SWEPT_BODY",BODY,{"disambiguationData":[OSD([sQuery(id+"F27.wireOp",EDGE,"E61")])]});
            var Q4;
            Q4=makeQuery(id+"F1.opExtrude","SWEPT_BODY",BODY,{"disambiguationData":[OSD([sQuery(id+"F0.wireOp",EDGE,"E1.bottom"),sQuery(id+"F0.wireOp",EDGE,"E1.top"),sQuery(id+"F0.wireOp",EDGE,"E1.left"),sQuery(id+"F0.wireOp",EDGE,"E1.right"),sQuery(id+"F0.wireOp",EDGE,"E2.bottom"),sQuery(id+"F0.wireOp",EDGE,"E2.top"),sQuery(id+"F0.wireOp",EDGE,"E2.left"),sQuery(id+"F0.wireOp",EDGE,"E2.right"),sQuery(id+"F0.wireOp",EDGE,"E3.filletArc"),sQuery(id+"F0.wireOp",EDGE,"E4.filletArc"),sQuery(id+"F0.wireOp",EDGE,"E5.filletArc"),sQuery(id+"F0.wireOp",EDGE,"E6.filletArc"),sQuery(id+"F0.wireOp",EDGE,"E11.filletArc"),sQuery(id+"F0.wireOp",EDGE,"E12.filletArc"),sQuery(id+"F0.wireOp",EDGE,"E13.filletArc"),sQuery(id+"F0.wireOp",EDGE,"E14.filletArc")])]});
            booleanBodies(context, id + "F29", {"operationType" : BooleanOperationType.SUBTRACTION, "tools" : qUnion([Q0, Q1, Q2, Q3]), "targets" : qUnion([Q4])});
        }
    });
